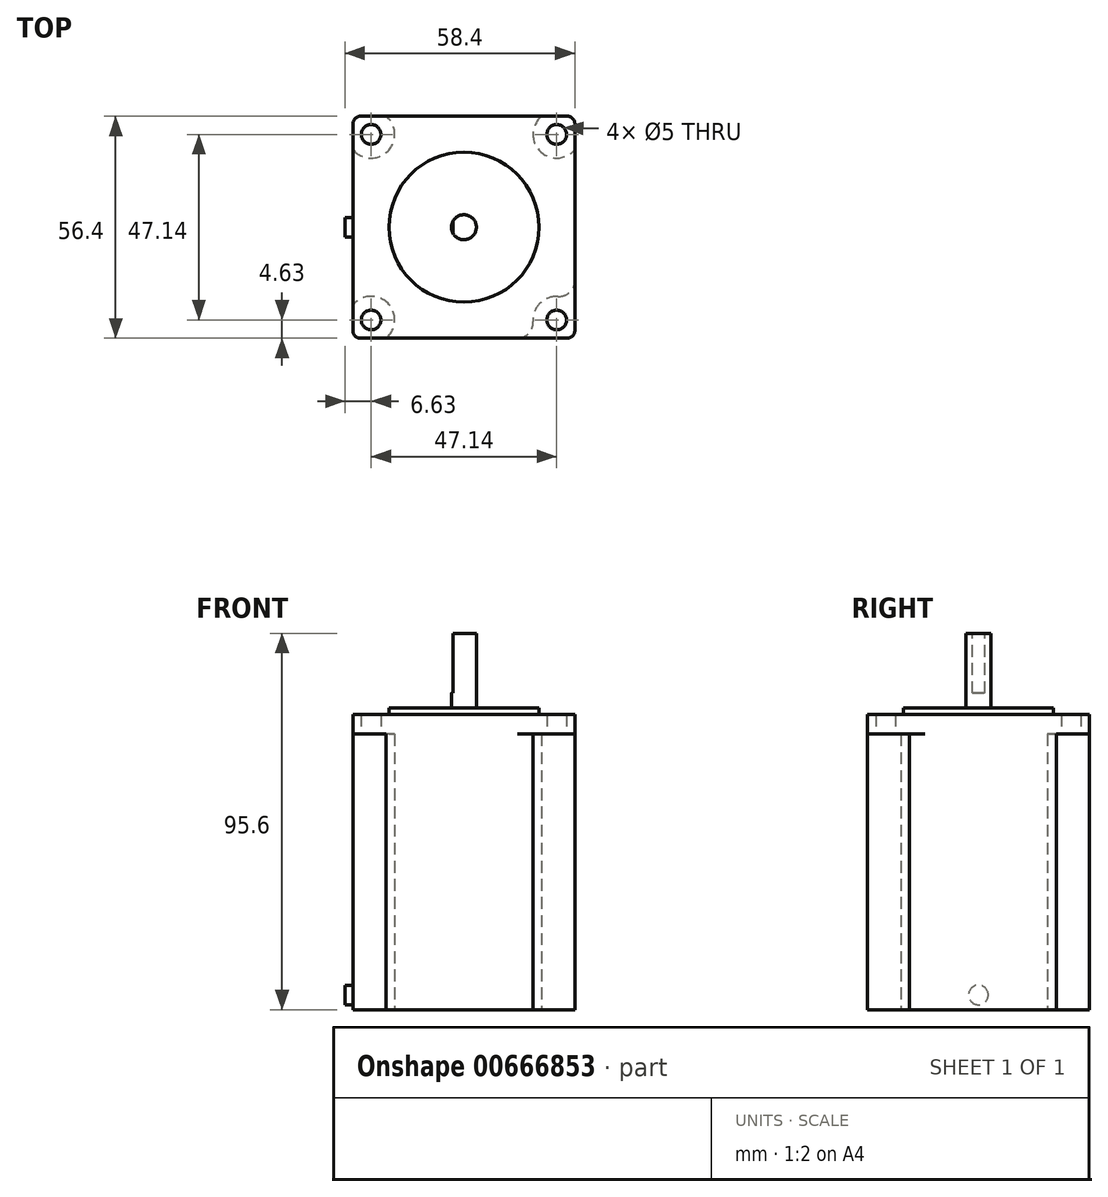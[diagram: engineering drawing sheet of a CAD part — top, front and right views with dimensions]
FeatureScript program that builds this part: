
annotation { "Feature Type Name" : "Feature", "Feature Type Description" : "" }
export const myFeature = defineFeature(function(context is Context, id is Id, definition is map)
    precondition{}
    {
        {
            var Q0;
            Q0=qCreatedBy(makeId("Top.planeOp"),FACE);
            var sketch = newSketch(context, id + "F0", { "sketchPlane" : qUnion([Q0])});
            skLineSegment(sketch, "E0.bottom", {"start": v(28.2, -28.2) * mm, "end": v(-28.2, -28.2) * mm});
            skLineSegment(sketch, "E0.top", {"start": v(28.2, 28.2) * mm, "end": v(-28.2, 28.2) * mm});
            skLineSegment(sketch, "E0.left", {"start": v(28.2, -28.2) * mm, "end": v(28.2, 28.2) * mm});
            skLineSegment(sketch, "E0.right", {"start": v(-28.2, -28.2) * mm, "end": v(-28.2, 28.2) * mm});
            skPoint(sketch, "E0.middle", {"position": v(0, 0) * mm});
            skCircle(sketch, "E1", {"center": v(-23.57, 23.57) * mm, "radius": 2.5 * mm});
            skCircle(sketch, "E2.0.1.0", {"center": v(-23.57, -23.57) * mm, "radius": 2.5 * mm});
            skCircle(sketch, "E2.1.0.0", {"center": v(23.57, 23.57) * mm, "radius": 2.5 * mm});
            skCircle(sketch, "E2.1.1.0", {"center": v(23.57, -23.57) * mm, "radius": 2.5 * mm});
            skLineSegment(sketch, "E2.direction1", {"start": v(-23.57, 23.57) * mm, "end": v(23.57, 23.57) * mm, "construction": true});
            skLineSegment(sketch, "E2.direction2", {"start": v(-23.57, 23.57) * mm, "end": v(-23.57, -23.57) * mm, "construction": true});
            skLineSegment(sketch, "E3", {"start": v(0, 0) * mm, "end": v(-23.57, 23.57) * mm, "construction": true});
            skLineSegment(sketch, "E4", {"start": v(0, 0) * mm, "end": v(23.57, 23.57) * mm, "construction": true});
            skLineSegment(sketch, "E5", {"start": v(0, 0) * mm, "end": v(-23.57, -23.57) * mm, "construction": true});
            skSolve(sketch);
        }
        {
            var Q0;
            Q0=makeQuery(id+"F0.imprint","IMPRINT",FACE,{"disambiguationData":[TD([[makeQuery(id+"F0.imprint","IMPRINT",EDGE,{"derivedFrom":sQuery(id+"F0.wireOp",EDGE,"E0.bottom")}),-1.0]])]});
            extrude(context, id + "F1", {"entities" : qUnion([Q0]), "depth" : 75 * mm, "offsetDistance" : 25 * mm});
        }
        {
            var Q0;
            Q0=makeQuery(id+"F1.opExtrude","CAP_FACE",FACE,{"disambiguationData":[OSD([sQuery(id+"F0.wireOp",EDGE,"E0.bottom"),sQuery(id+"F0.wireOp",EDGE,"E0.top"),sQuery(id+"F0.wireOp",EDGE,"E0.left"),sQuery(id+"F0.wireOp",EDGE,"E0.right"),sQuery(id+"F0.wireOp",EDGE,"E1"),sQuery(id+"F0.wireOp",EDGE,"E2.0.1.0"),sQuery(id+"F0.wireOp",EDGE,"E2.1.0.0"),sQuery(id+"F0.wireOp",EDGE,"E2.1.1.0")])],"isStart":false});
            var sketch = newSketch(context, id + "F2", { "sketchPlane" : qUnion([Q0])});
            skCircle(sketch, "E6", {"center": v(0, 0) * mm, "radius": 19.05 * mm});
            skSolve(sketch);
        }
        {
            var Q0;
            Q0=makeQuery(id+"F2.imprint","IMPRINT",FACE,{"disambiguationData":[TD([[makeQuery(id+"F2.imprint","IMPRINT",EDGE,{"derivedFrom":sQuery(id+"F2.wireOp",EDGE,"E6")}),1.0]])]});
            extrude(context, id + "F3", {"entities" : qUnion([Q0]), "operationType" : NewBodyOperationType.ADD, "depth" : 1.6 * mm, "offsetDistance" : 25 * mm});
        }
        {
            var Q0;
            Q0=makeQuery(id+"F3.opExtrude","CAP_FACE",FACE,{"disambiguationData":[OSD([sQuery(id+"F2.wireOp",EDGE,"E6")])],"isStart":false});
            var sketch = newSketch(context, id + "F4", { "sketchPlane" : qUnion([Q0])});
            skCircle(sketch, "E7", {"center": v(0, 0) * mm, "radius": 3.18 * mm});
            skSolve(sketch);
        }
        {
            var Q0;
            Q0=makeQuery(id+"F4.imprint","IMPRINT",FACE,{"disambiguationData":[TD([[makeQuery(id+"F4.imprint","IMPRINT",EDGE,{"derivedFrom":sQuery(id+"F4.wireOp",EDGE,"E7")}),1.0]])]});
            extrude(context, id + "F5", {"entities" : qUnion([Q0]), "depth" : 19 * mm, "offsetDistance" : 25 * mm});
        }
        {
            var Q0;
            Q0=makeQuery(id+"F1.opExtrude","SWEPT_FACE",FACE,{"disambiguationData":[OSD([sQuery(id+"F0.wireOp",EDGE,"E0.right")])]});
            var sketch = newSketch(context, id + "F6", { "sketchPlane" : qUnion([Q0])});
            skCircle(sketch, "E8", {"center": v(0, 3.73) * mm, "radius": 2.5 * mm});
            skSolve(sketch);
        }
        {
            var Q0;
            Q0=makeQuery(id+"F6.imprint","IMPRINT",FACE,{"disambiguationData":[TD([[makeQuery(id+"F6.imprint","IMPRINT",EDGE,{"derivedFrom":sQuery(id+"F6.wireOp",EDGE,"E8")}),1.0]])]});
            extrude(context, id + "F7", {"entities" : qUnion([Q0]), "operationType" : NewBodyOperationType.ADD, "depth" : 2 * mm, "offsetDistance" : 25 * mm});
        }
        {
            var Q0;
            Q0=makeQuery(id+"F1.opExtrude","SWEPT_EDGE",EDGE,{"disambiguationData":[OSD([sQuery(id+"F0.wireOp",EDGE,"E0.top"),sQuery(id+"F0.wireOp",EDGE,"E0.right")])]});
            var Q1;
            Q1=makeQuery(id+"F1.opExtrude","SWEPT_EDGE",EDGE,{"disambiguationData":[OSD([sQuery(id+"F0.wireOp",EDGE,"E0.top"),sQuery(id+"F0.wireOp",EDGE,"E0.left")])]});
            var Q2;
            Q2=makeQuery(id+"F1.opExtrude","SWEPT_EDGE",EDGE,{"disambiguationData":[OSD([sQuery(id+"F0.wireOp",EDGE,"E0.bottom"),sQuery(id+"F0.wireOp",EDGE,"E0.left")])]});
            var Q3;
            Q3=makeQuery(id+"F1.opExtrude","SWEPT_EDGE",EDGE,{"disambiguationData":[OSD([sQuery(id+"F0.wireOp",EDGE,"E0.bottom"),sQuery(id+"F0.wireOp",EDGE,"E0.right")])]});
            fillet(context, id + "F8", {"entities" : qUnion([Q0, Q1, Q2, Q3]), "radius" : 2 * mm, "tangentPropagation" : true, "allowEdgeOverflow" : false});
        }
        {
            var Q0;
            Q0=makeQuery(id+"F5.opExtrude","CAP_FACE",FACE,{"disambiguationData":[OSD([sQuery(id+"F4.wireOp",EDGE,"E7")])],"isStart":false});
            var sketch = newSketch(context, id + "F9", { "sketchPlane" : qUnion([Q0])});
            skLineSegment(sketch, "E9", {"start": v(-2.74, -1.6) * mm, "end": v(-2.74, 1.6) * mm});
            skSolve(sketch);
        }
        {
            var Q0;
            {var subQ0=sQuery(id+"F9.wireOp",EDGE,"E9");Q0=makeQuery(id+"F9.imprint","IMPRINT",FACE,{"disambiguationData":[TD([[makeQuery(id+"F9.imprint","IMPRINT",EDGE,{"derivedFrom":subQ0}),1.0]])]});}
            extrude(context, id + "F10", {"entities" : qUnion([Q0]), "operationType" : NewBodyOperationType.REMOVE, "oppositeDirection" : true, "depth" : 15.15 * mm, "offsetDistance" : 25 * mm});
        }
        {
            var Q0;
            Q0=makeQuery(id+"F1.opExtrude","CAP_FACE",FACE,{"disambiguationData":[OSD([sQuery(id+"F0.wireOp",EDGE,"E0.bottom"),sQuery(id+"F0.wireOp",EDGE,"E0.top"),sQuery(id+"F0.wireOp",EDGE,"E0.left"),sQuery(id+"F0.wireOp",EDGE,"E0.right"),sQuery(id+"F0.wireOp",EDGE,"E1"),sQuery(id+"F0.wireOp",EDGE,"E2.0.1.0"),sQuery(id+"F0.wireOp",EDGE,"E2.1.0.0"),sQuery(id+"F0.wireOp",EDGE,"E2.1.1.0")])],"isStart":true});
            var sketch = newSketch(context, id + "F11", { "sketchPlane" : qUnion([Q0])});
            skCircle(sketch, "E10", {"center": v(-23.57, 23.57) * mm, "radius": 6 * mm});
            skCircle(sketch, "E11.0.1.0", {"center": v(-23.57, -23.57) * mm, "radius": 6 * mm});
            skCircle(sketch, "E11.1.0.0", {"center": v(23.57, 23.57) * mm, "radius": 6 * mm});
            skCircle(sketch, "E11.1.1.0", {"center": v(23.57, -23.57) * mm, "radius": 6 * mm});
            skLineSegment(sketch, "E11.direction1", {"start": v(-23.57, 23.57) * mm, "end": v(23.57, 23.57) * mm, "construction": true});
            skLineSegment(sketch, "E11.direction2", {"start": v(-23.57, 23.57) * mm, "end": v(-23.57, -23.57) * mm, "construction": true});
            skSolve(sketch);
        }
        {
            var Q0;
            {var subQ0=sQuery(id+"F0.wireOp",EDGE,"E2.0.1.0");Q0=makeQuery(id+"F11.imprint","IMPRINT",FACE,{"disambiguationData":[TD([[makeQuery(id+"F11.imprint","IMPRINT",EDGE,{"derivedFrom":makeQuery(id+"F1.opExtrude","CAP_EDGE",EDGE,{"disambiguationData":[OSD([subQ0])],"isStart":true})}),1.0]])]});}
            var Q1;
            {var subQ0=sQuery(id+"F0.wireOp",EDGE,"E2.1.1.0");Q1=makeQuery(id+"F11.imprint","IMPRINT",FACE,{"disambiguationData":[TD([[makeQuery(id+"F11.imprint","IMPRINT",EDGE,{"derivedFrom":makeQuery(id+"F1.opExtrude","CAP_EDGE",EDGE,{"disambiguationData":[OSD([subQ0])],"isStart":true})}),1.0]])]});}
            var Q2;
            {var subQ0=sQuery(id+"F11.wireOp",EDGE,"E11.1.0.0");var subQ1=sQuery(id+"F0.wireOp",EDGE,"E0.bottom");var subQ2=makeQuery(id+"F1.opExtrude","CAP_EDGE",EDGE,{"disambiguationData":[OSD([subQ1])],"isStart":true});var subQ3=makeQuery(id+"F11.imprint","INTERSECT",VERTEX,{"derivedFrom":[subQ2,subQ0]});Q2=makeQuery(id+"F11.imprint","IMPRINT",FACE,{"disambiguationData":[TD([[makeQuery(id+"F11.imprint","IMPRINT",EDGE,{"disambiguationData":[TD([[subQ3,1.0]])],"derivedFrom":subQ0}),1.0]])]});}
            var Q3;
            {var subQ2=sQuery(id+"F0.wireOp",EDGE,"E2.1.0.0");Q3=makeQuery(id+"F11.imprint","IMPRINT",FACE,{"disambiguationData":[TD([[makeQuery(id+"F11.imprint","IMPRINT",EDGE,{"derivedFrom":makeQuery(id+"F1.opExtrude","CAP_EDGE",EDGE,{"disambiguationData":[OSD([subQ2])],"isStart":true})}),1.0]])]});}
            var Q4;
            {var subQ2=sQuery(id+"F0.wireOp",EDGE,"E1");Q4=makeQuery(id+"F11.imprint","IMPRINT",FACE,{"disambiguationData":[TD([[makeQuery(id+"F11.imprint","IMPRINT",EDGE,{"derivedFrom":makeQuery(id+"F1.opExtrude","CAP_EDGE",EDGE,{"disambiguationData":[OSD([subQ2])],"isStart":true})}),1.0]])]});}
            extrude(context, id + "F12", {"entities" : qUnion([Q0, Q1, Q2, Q3, Q4]), "operationType" : NewBodyOperationType.REMOVE, "oppositeDirection" : true, "depth" : 70 * mm, "offsetDistance" : 25 * mm});
        }
        {
            var Q0;
            Q0=makeQuery(id+"F12.boolean.opBoolean","COPY",EDGE,{"derivedFrom":makeQuery(id+"F12.opExtrude","SWEPT_EDGE",EDGE,{"disambiguationData":[OSD([sQuery(id+"F0.wireOp",EDGE,"E0.right"),sQuery(id+"F11.wireOp",EDGE,"E11.0.1.0")])]})});
            var Q1;
            Q1=makeQuery(id+"F12.boolean.opBoolean","COPY",EDGE,{"derivedFrom":makeQuery(id+"F12.opExtrude","SWEPT_EDGE",EDGE,{"disambiguationData":[OSD([sQuery(id+"F0.wireOp",EDGE,"E0.top"),sQuery(id+"F11.wireOp",EDGE,"E11.0.1.0")])]})});
            var Q2;
            Q2=makeQuery(id+"F12.boolean.opBoolean","COPY",EDGE,{"derivedFrom":makeQuery(id+"F12.opExtrude","SWEPT_EDGE",EDGE,{"disambiguationData":[OSD([sQuery(id+"F0.wireOp",EDGE,"E0.right"),sQuery(id+"F11.wireOp",EDGE,"E10")])]})});
            var Q3;
            Q3=makeQuery(id+"F12.boolean.opBoolean","COPY",EDGE,{"derivedFrom":makeQuery(id+"F12.opExtrude","SWEPT_EDGE",EDGE,{"disambiguationData":[OSD([sQuery(id+"F0.wireOp",EDGE,"E0.bottom"),sQuery(id+"F11.wireOp",EDGE,"E10")])]})});
            var Q4;
            Q4=makeQuery(id+"F12.boolean.opBoolean","INTERSECT",EDGE,{"derivedFrom":[makeQuery(id+"F1.opExtrude","SWEPT_FACE",FACE,{"disambiguationData":[OSD([sQuery(id+"F0.wireOp",EDGE,"E0.bottom")])]}),makeQuery(id+"F12.opExtrude","SWEPT_FACE",FACE,{"disambiguationData":[OSD([sQuery(id+"F11.wireOp",EDGE,"E11.1.0.0")])]})]});
            var Q5;
            Q5=makeQuery(id+"F12.boolean.opBoolean","INTERSECT",EDGE,{"derivedFrom":[makeQuery(id+"F1.opExtrude","SWEPT_FACE",FACE,{"disambiguationData":[OSD([sQuery(id+"F0.wireOp",EDGE,"E0.left")])]}),makeQuery(id+"F12.opExtrude","SWEPT_FACE",FACE,{"disambiguationData":[OSD([sQuery(id+"F11.wireOp",EDGE,"E11.1.0.0")])]})]});
            var Q6;
            Q6=makeQuery(id+"F12.boolean.opBoolean","COPY",EDGE,{"derivedFrom":makeQuery(id+"F12.opExtrude","SWEPT_EDGE",EDGE,{"disambiguationData":[OSD([sQuery(id+"F0.wireOp",EDGE,"E0.left"),sQuery(id+"F11.wireOp",EDGE,"E11.1.1.0")])]})});
            var Q7;
            Q7=makeQuery(id+"F12.boolean.opBoolean","COPY",EDGE,{"derivedFrom":makeQuery(id+"F12.opExtrude","SWEPT_EDGE",EDGE,{"disambiguationData":[OSD([sQuery(id+"F0.wireOp",EDGE,"E0.top"),sQuery(id+"F11.wireOp",EDGE,"E11.1.1.0")])]})});
            fillet(context, id + "F13", {"entities" : qUnion([Q0, Q1, Q2, Q3, Q4, Q5, Q6, Q7]), "radius" : 4 * mm, "tangentPropagation" : true, "allowEdgeOverflow" : false});
        }
    });
